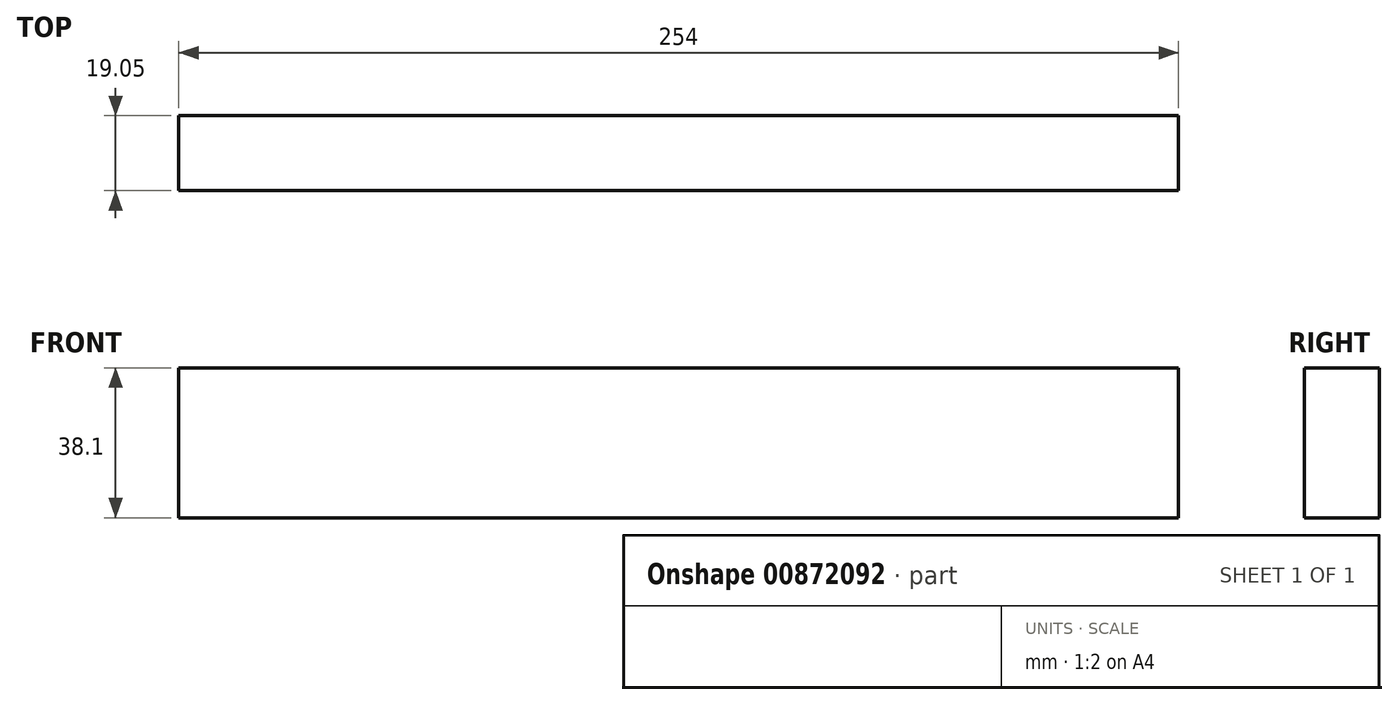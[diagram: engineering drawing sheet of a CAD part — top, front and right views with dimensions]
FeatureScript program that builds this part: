
annotation { "Feature Type Name" : "Feature", "Feature Type Description" : "" }
export const myFeature = defineFeature(function(context is Context, id is Id, definition is map)
    precondition{}
    {
        {
            var Q0;
            Q0=qCreatedBy(makeId("Front.planeOp"),FACE);
            var sketch = newSketch(context, id + "F0", { "sketchPlane" : qUnion([Q0])});
            skLineSegment(sketch, "E0.bottom", {"start": v(0, 0) * mm, "end": v(254, 0) * mm});
            skLineSegment(sketch, "E0.top", {"start": v(0, 38.1) * mm, "end": v(254, 38.1) * mm});
            skLineSegment(sketch, "E0.left", {"start": v(0, 0) * mm, "end": v(0, 38.1) * mm});
            skLineSegment(sketch, "E0.right", {"start": v(254, 0) * mm, "end": v(254, 38.1) * mm});
            skSolve(sketch);
        }
        {
            var Q0;
            Q0=qSketchRegion(id+"F0",true);
            extrude(context, id + "F1", {"entities" : qUnion([Q0]), "depth" : 19.05 * mm});
        }
    });
